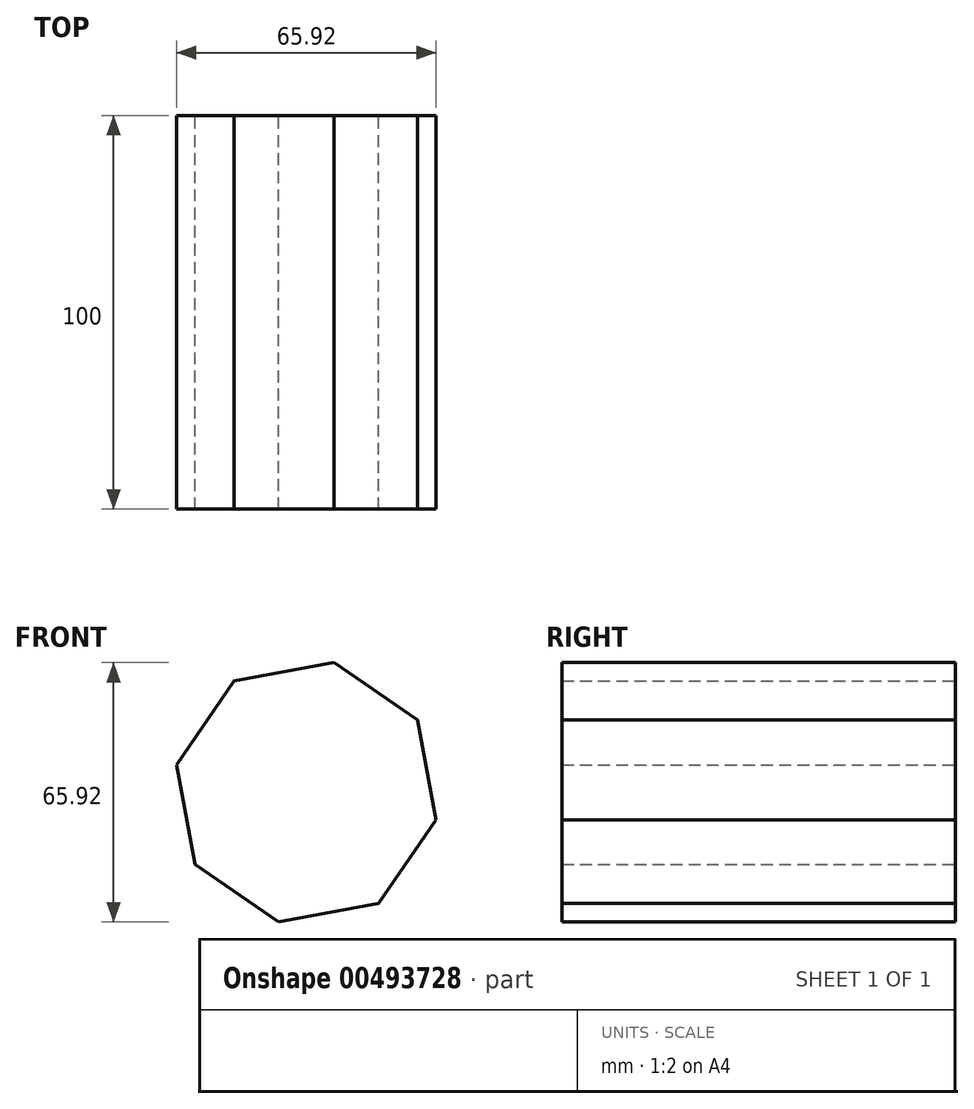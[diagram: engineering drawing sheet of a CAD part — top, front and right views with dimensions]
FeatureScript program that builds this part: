
annotation { "Feature Type Name" : "Feature", "Feature Type Description" : "" }
export const myFeature = defineFeature(function(context is Context, id is Id, definition is map)
    precondition{}
    {
        {
            var Q0;
            Q0=qCreatedBy(makeId("Front.planeOp"),FACE);
            var sketch = newSketch(context, id + "F0", { "sketchPlane" : qUnion([Q0])});
            skCircle(sketch, "E0.cCircle", {"center": v(0, 0) * mm, "radius": 33.7 * mm, "construction": true});
            skLineSegment(sketch, "E0.0", {"start": v(-28.26, -18.36) * mm, "end": v(-32.96, 7) * mm});
            skLineSegment(sketch, "E0.1", {"start": v(-32.96, 7) * mm, "end": v(-18.36, 28.26) * mm});
            skLineSegment(sketch, "E0.2", {"start": v(-18.36, 28.26) * mm, "end": v(7, 32.96) * mm});
            skLineSegment(sketch, "E0.3", {"start": v(7, 32.96) * mm, "end": v(28.26, 18.36) * mm});
            skLineSegment(sketch, "E0.4", {"start": v(28.26, 18.36) * mm, "end": v(32.96, -7) * mm});
            skLineSegment(sketch, "E0.5", {"start": v(32.96, -7) * mm, "end": v(18.36, -28.26) * mm});
            skLineSegment(sketch, "E0.6", {"start": v(18.36, -28.26) * mm, "end": v(-7, -32.96) * mm});
            skLineSegment(sketch, "E0.7", {"start": v(-7, -32.96) * mm, "end": v(-28.26, -18.36) * mm});
            skSolve(sketch);
        }
        {
            var Q0;
            Q0=makeQuery(id+"F0.imprint","IMPRINT",FACE,{"disambiguationData":[TD([[makeQuery(id+"F0.imprint","IMPRINT",EDGE,{"derivedFrom":sQuery(id+"F0.wireOp",EDGE,"E0.0")}),-1.0]])]});
            extrude(context, id + "F1", {"entities" : qUnion([Q0]), "depth" : 100 * mm});
        }
    });
